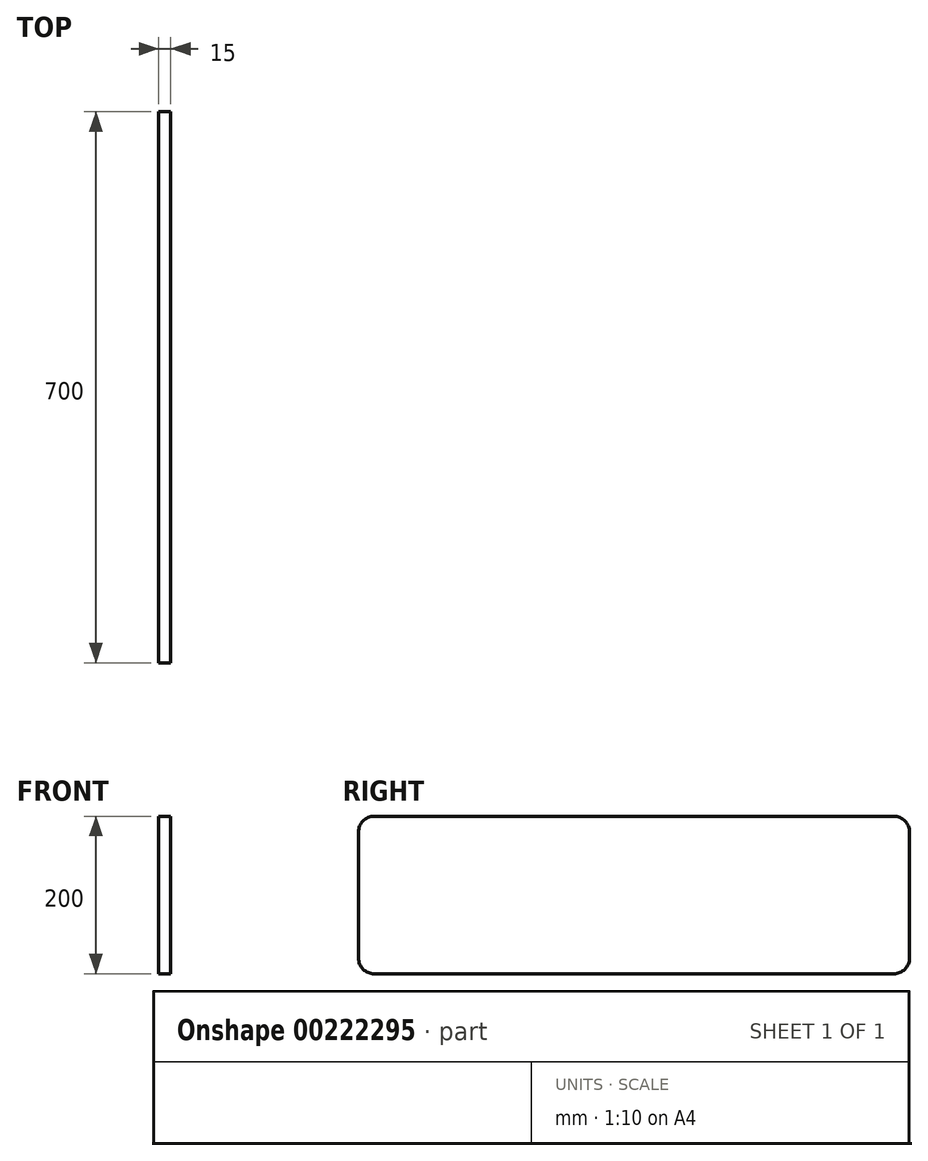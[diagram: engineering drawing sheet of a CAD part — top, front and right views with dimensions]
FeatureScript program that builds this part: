
annotation { "Feature Type Name" : "Feature", "Feature Type Description" : "" }
export const myFeature = defineFeature(function(context is Context, id is Id, definition is map)
    precondition{}
    {
        {
            var Q0;
            Q0=qCreatedBy(makeId("Right.planeOp"),FACE);
            var sketch = newSketch(context, id + "F0", { "sketchPlane" : qUnion([Q0])});
            skLineSegment(sketch, "E0.bottom", {"start": v(350, 100) * mm, "end": v(-350, 100) * mm});
            skLineSegment(sketch, "E0.top", {"start": v(350, -100) * mm, "end": v(-350, -100) * mm});
            skLineSegment(sketch, "E0.left", {"start": v(350, 100) * mm, "end": v(350, -100) * mm});
            skLineSegment(sketch, "E0.right", {"start": v(-350, 100) * mm, "end": v(-350, -100) * mm});
            skPoint(sketch, "E0.middle", {"position": v(0, 0) * mm});
            skSolve(sketch);
        }
        {
            var Q0;
            Q0 = qSketchRegion(id + "F0", true);
            extrude(context, id + "F1", {"entities" : qUnion([Q0]), "depth" : 15 * mm, "offsetDistance" : 25 * mm});
        }
        {
            var Q0;
            Q0=makeQuery(id+"F1.opExtrude","SWEPT_EDGE",EDGE,{"disambiguationData":[OSD([sQuery(id+"F0.wireOp",EDGE,"E0.bottom"),sQuery(id+"F0.wireOp",EDGE,"E0.left")])]});
            var Q1;
            Q1=makeQuery(id+"F1.opExtrude","SWEPT_EDGE",EDGE,{"disambiguationData":[OSD([sQuery(id+"F0.wireOp",EDGE,"E0.top"),sQuery(id+"F0.wireOp",EDGE,"E0.left")])]});
            var Q2;
            Q2=makeQuery(id+"F1.opExtrude","SWEPT_EDGE",EDGE,{"disambiguationData":[OSD([sQuery(id+"F0.wireOp",EDGE,"E0.top"),sQuery(id+"F0.wireOp",EDGE,"E0.right")])]});
            var Q3;
            Q3=makeQuery(id+"F1.opExtrude","SWEPT_EDGE",EDGE,{"disambiguationData":[OSD([sQuery(id+"F0.wireOp",EDGE,"E0.bottom"),sQuery(id+"F0.wireOp",EDGE,"E0.right")])]});
            fillet(context, id + "F2", {"entities" : qUnion([Q0, Q1, Q2, Q3]), "radius" : 20 * mm, "tangentPropagation" : true, "allowEdgeOverflow" : false});
        }
    });
